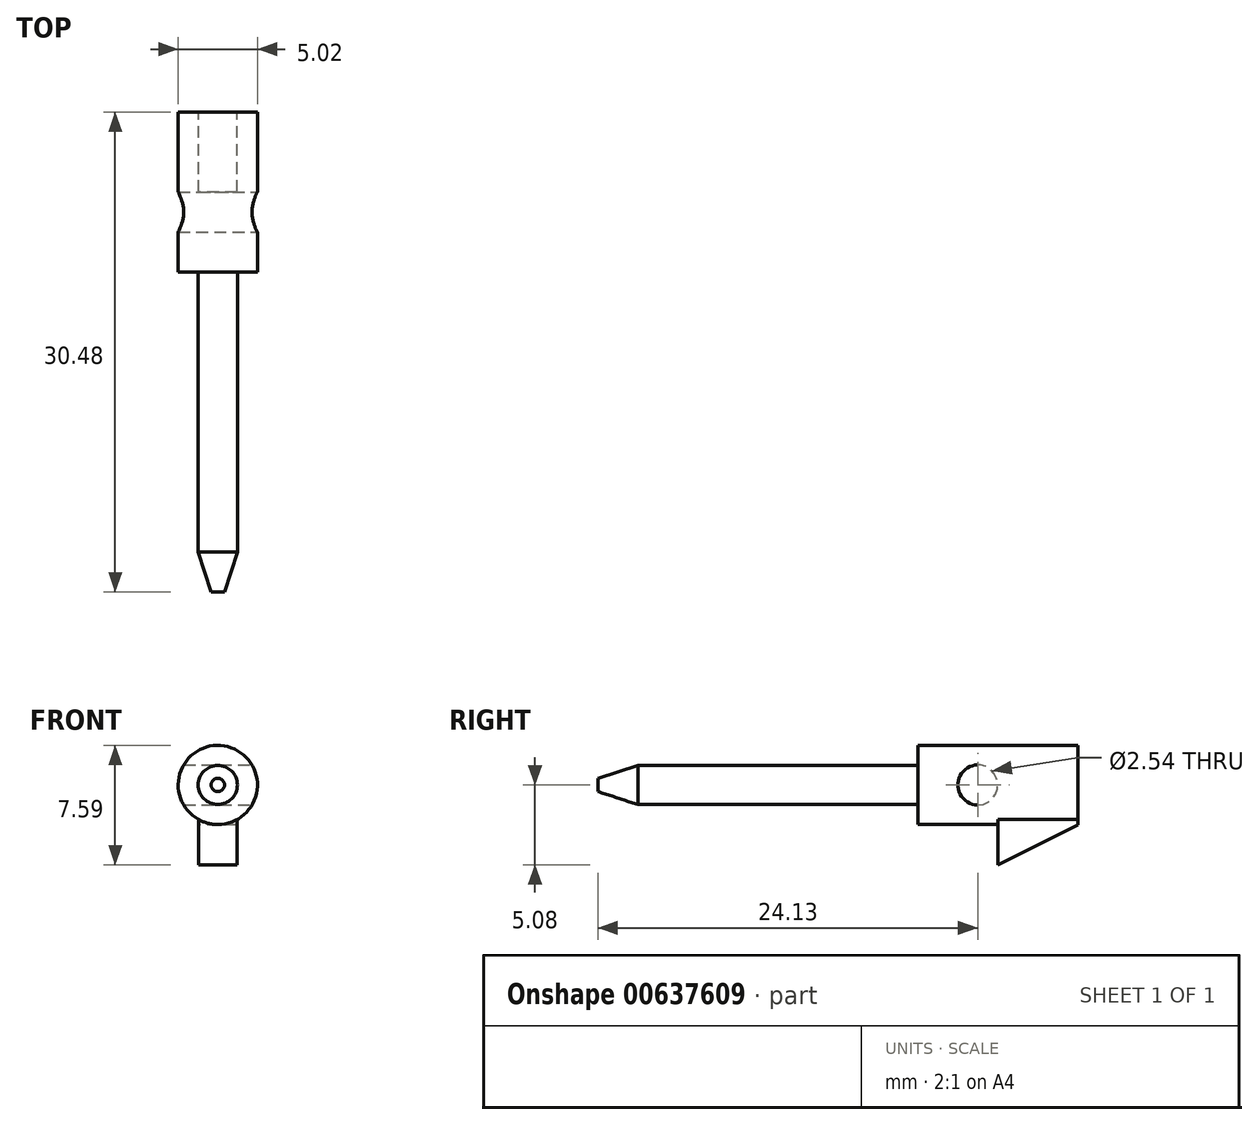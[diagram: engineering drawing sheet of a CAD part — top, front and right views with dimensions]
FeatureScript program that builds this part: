
annotation { "Feature Type Name" : "Feature", "Feature Type Description" : "" }
export const myFeature = defineFeature(function(context is Context, id is Id, definition is map)
    precondition{}
    {
        {
            var Q0;
            Q0=qCreatedBy(makeId("Front.planeOp"),FACE);
            var sketch = newSketch(context, id + "F0", { "sketchPlane" : qUnion([Q0])});
            skCircle(sketch, "E0", {"center": v(0, 0) * mm, "radius": 2.51 * mm});
            skSolve(sketch);
        }
        {
            var Q0;
            Q0=makeQuery(id+"F0.imprint","IMPRINT",FACE,{"disambiguationData":[TD([[makeQuery(id+"F0.imprint","IMPRINT",EDGE,{"derivedFrom":sQuery(id+"F0.wireOp",EDGE,"E0")}),1.0]])]});
            extrude(context, id + "F1", {"entities" : qUnion([Q0]), "depth" : 10.16 * mm});
        }
        {
            var Q0;
            Q0=makeQuery(id+"F1.opExtrude","CAP_FACE",FACE,{"disambiguationData":[OSD([sQuery(id+"F0.wireOp",EDGE,"E0")])],"isStart":false});
            var sketch = newSketch(context, id + "F2", { "sketchPlane" : qUnion([Q0])});
            skCircle(sketch, "E1", {"center": v(0, 0) * mm, "radius": 1.24 * mm});
            skSolve(sketch);
        }
        {
            var Q0;
            Q0=qSketchRegion(id+"F2",true);
            var Q1;
            Q1=makeQuery(id+"F2.imprint","IMPRINT",FACE,{"disambiguationData":[TD([[makeQuery(id+"F2.imprint","IMPRINT",EDGE,{"derivedFrom":sQuery(id+"F2.wireOp",EDGE,"E1")}),1.0]])]});
            extrude(context, id + "F3", {"entities" : qUnion([Q0, Q1]), "operationType" : NewBodyOperationType.ADD, "depth" : 17.78 * mm});
        }
        {
            var Q0;
            Q0=makeQuery(id+"F3.opExtrude","CAP_FACE",FACE,{"disambiguationData":[OSD([sQuery(id+"F2.wireOp",EDGE,"E1")])],"isStart":false});
            cPlane(context, id + "F4", {"entities" : qUnion([Q0]), "cplaneType" : CPlaneType.OFFSET, "offset" : 2.54 * mm, "width" : 152.4 * mm, "height" : 152.4 * mm});
        }
        {
            var Q0;
            Q0=qCreatedBy(id+"F4.planeOp",FACE);
            var sketch = newSketch(context, id + "F5", { "sketchPlane" : qUnion([Q0])});
            skCircle(sketch, "E2", {"center": v(0, 0) * mm, "radius": 0.42 * mm});
            skSolve(sketch);
        }
        {
            var Q1;
            Q1=makeQuery(id+"F3.opExtrude","CAP_FACE",FACE,{"disambiguationData":[OSD([sQuery(id+"F2.wireOp",EDGE,"E1")])],"isStart":false});
            var Q2;
            Q2=makeQuery(id+"F5.imprint","IMPRINT",FACE,{"disambiguationData":[TD([[makeQuery(id+"F5.imprint","IMPRINT",EDGE,{"derivedFrom":sQuery(id+"F5.wireOp",EDGE,"E2")}),1.0]])]});
            loft(context, id + "F6", {"operationType" : NewBodyOperationType.ADD, "sheetProfilesArray" : [{ "sheetProfileEntities" : qUnion([Q1]) }, { "sheetProfileEntities" : qUnion([Q2]) }]});
        }
        {
            var Q0;
            Q0=qCreatedBy(makeId("Right.planeOp"),FACE);
            var sketch = newSketch(context, id + "F7", { "sketchPlane" : qUnion([Q0])});
            skLineSegment(sketch, "E3", {"start": v(0, 0) * mm, "end": v(-6.35, 0) * mm});
            skCircle(sketch, "E4", {"center": v(-6.35, 0) * mm, "radius": 1.27 * mm});
            skSolve(sketch);
        }
        {
            var Q0;
            Q0=qSketchRegion(id+"F7",true);
            extrude(context, id + "F8", {"entities" : qUnion([Q0]), "operationType" : NewBodyOperationType.REMOVE, "oppositeDirection" : true, "depth" : 25.4 * mm});
        }
        {
            var Q0;
            Q0=qSketchRegion(id+"F7",true);
            extrude(context, id + "F9", {"entities" : qUnion([Q0]), "operationType" : NewBodyOperationType.REMOVE, "depth" : 25.4 * mm});
        }
        {
            var Q0;
            Q0=qCreatedBy(makeId("Right.planeOp"),FACE);
            var sketch = newSketch(context, id + "F10", { "sketchPlane" : qUnion([Q0])});
            skLineSegment(sketch, "E5", {"start": v(0, 0) * mm, "end": v(0, -2.54) * mm});
            skLineSegment(sketch, "E6", {"start": v(0, -2.54) * mm, "end": v(-5.08, -5.08) * mm});
            skLineSegment(sketch, "E7", {"start": v(-5.08, -5.08) * mm, "end": v(-5.08, -2.54) * mm});
            skLineSegment(sketch, "E8", {"start": v(-5.08, -2.54) * mm, "end": v(-5.08, 0) * mm});
            skLineSegment(sketch, "E9", {"start": v(-5.08, 0) * mm, "end": v(0, 0) * mm});
            skSolve(sketch);
        }
        {
            var Q0;
            Q0=qSketchRegion(id+"F10",true);
            extrude(context, id + "F11", {"entities" : qUnion([Q0]), "operationType" : NewBodyOperationType.ADD, "depth" : 1.22 * mm});
        }
        {
            var Q0;
            Q0=qSketchRegion(id+"F10",true);
            extrude(context, id + "F12", {"entities" : qUnion([Q0]), "operationType" : NewBodyOperationType.ADD, "oppositeDirection" : true, "depth" : 1.22 * mm});
        }
    });
